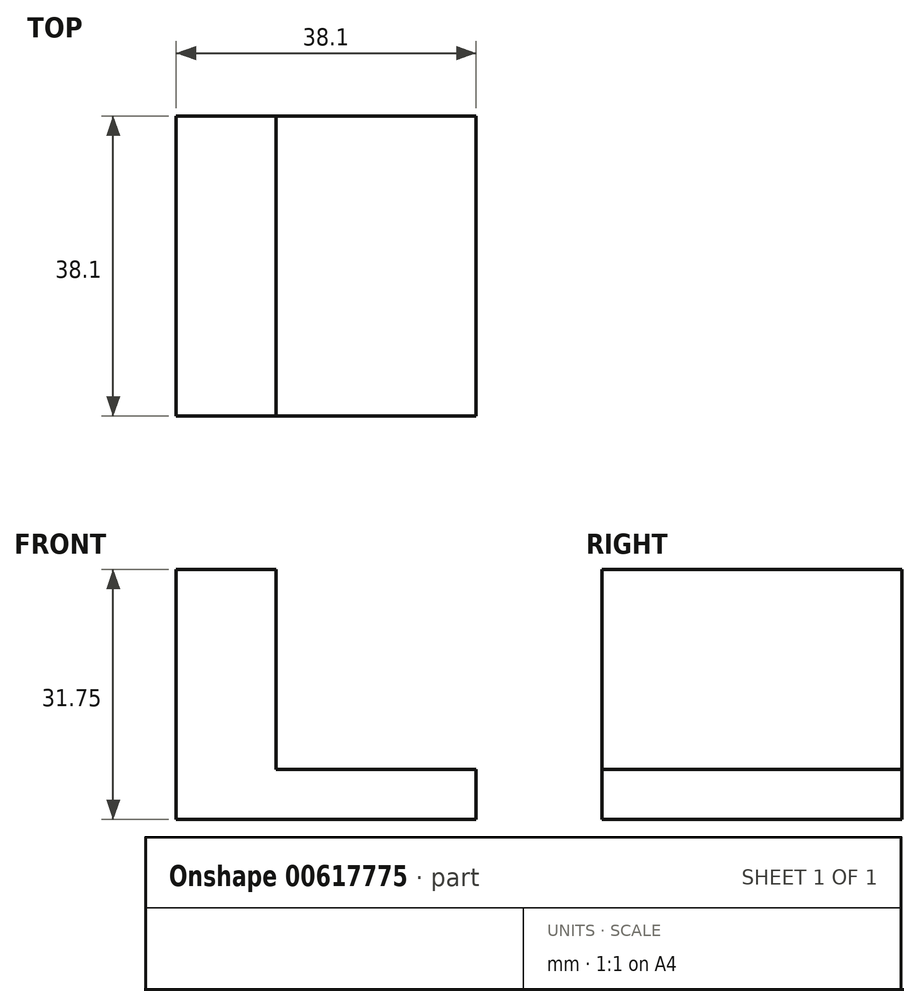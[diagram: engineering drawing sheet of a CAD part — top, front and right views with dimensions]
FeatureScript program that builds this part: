
annotation { "Feature Type Name" : "Feature", "Feature Type Description" : "" }
export const myFeature = defineFeature(function(context is Context, id is Id, definition is map)
    precondition{}
    {
        {
            var Q0;
            Q0=qCreatedBy(makeId("Front.planeOp"),FACE);
            var sketch = newSketch(context, id + "F0", { "sketchPlane" : qUnion([Q0])});
            skLineSegment(sketch, "E0", {"start": v(0, 31.75) * mm, "end": v(0, 0) * mm});
            skLineSegment(sketch, "E1", {"start": v(0, 0) * mm, "end": v(38.1, 0) * mm});
            skLineSegment(sketch, "E2", {"start": v(38.1, 0) * mm, "end": v(38.1, 6.35) * mm});
            skLineSegment(sketch, "E3", {"start": v(38.1, 6.35) * mm, "end": v(12.7, 6.35) * mm});
            skLineSegment(sketch, "E4", {"start": v(12.7, 6.35) * mm, "end": v(12.7, 31.75) * mm});
            skLineSegment(sketch, "E5", {"start": v(12.7, 31.75) * mm, "end": v(0, 31.75) * mm});
            skSolve(sketch);
        }
        {
            var Q0;
            Q0 = qSketchRegion(id + "F0", true);
            extrude(context, id + "F1", {"entities" : qUnion([Q0]), "depth" : 38.1 * mm, "offsetDistance" : 25.4 * mm});
        }
    });
